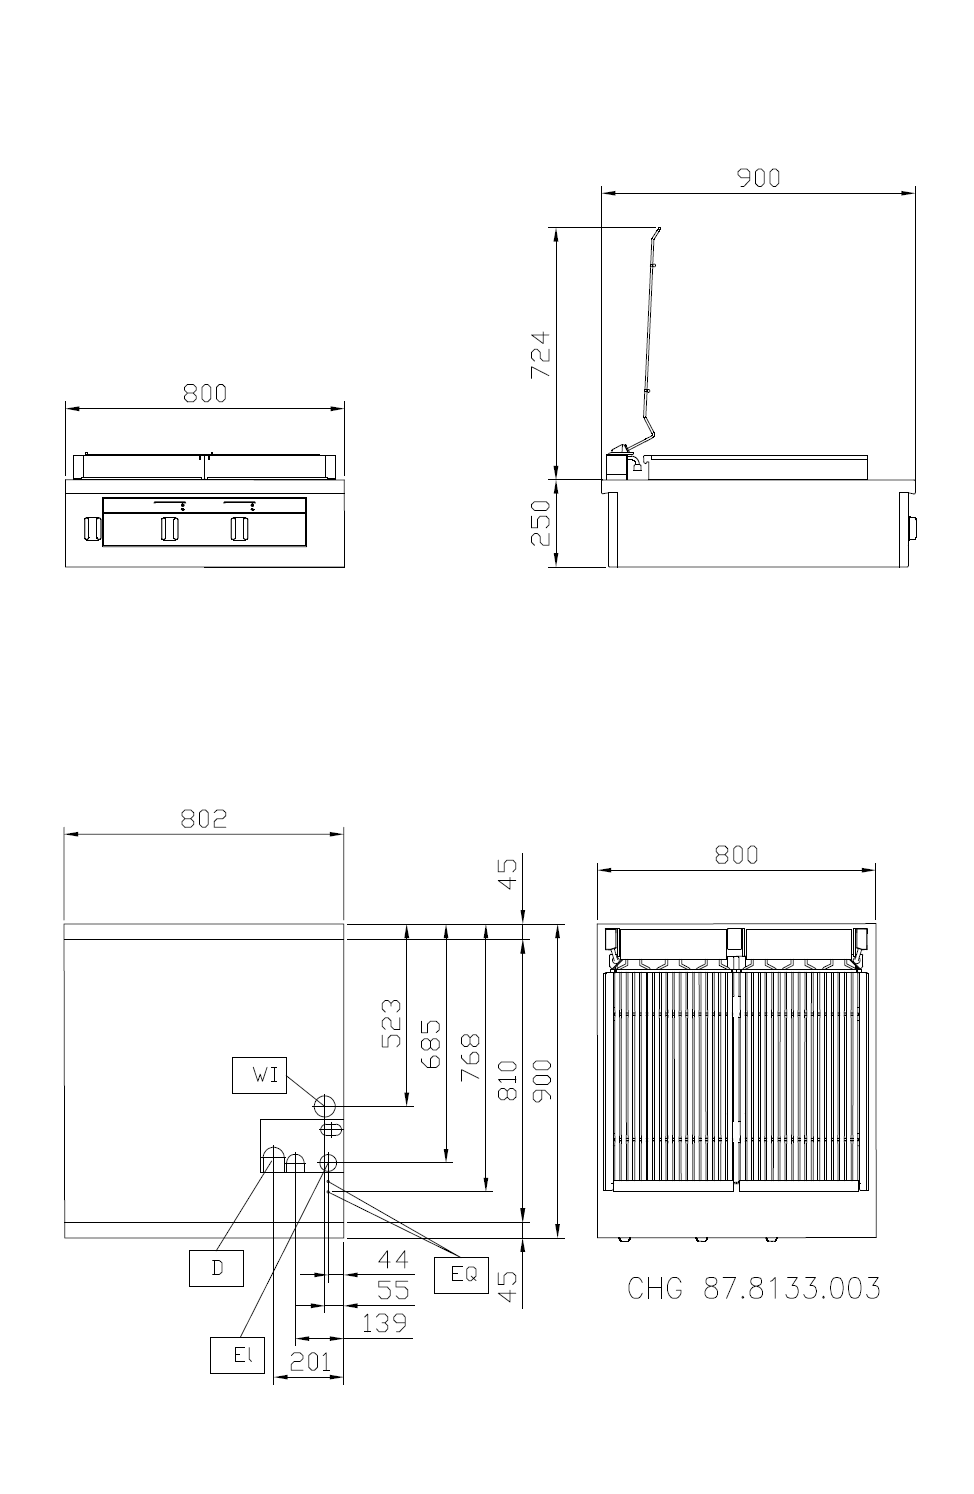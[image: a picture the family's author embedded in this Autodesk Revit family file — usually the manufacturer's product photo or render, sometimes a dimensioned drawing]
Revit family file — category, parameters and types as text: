
# Revit family: QF_ELECTROLUXPROFESSIONAL_589286_MCDEAAHOIO
name_source: partatom
category: Specialty Equipment
revit_build: Autodesk Revit 2018 (Build: 20190510_1515(x64)
units: mm (PartAtom-declared; Revit-internal decimal feet)

## family parameters
Always vertical = Yes
Cut with Voids When Loaded = No
Part Type = Normal
Room Calculation Point = No
Round Connector Dimension = Use Diameter
Shared = No
Work Plane-Based = No

## types (1)
- Standard
    Accessory = Yes
    Cold Water Size = 1"
    Compressed Air Pressure = 0.00 psi
    Compressed Air Size = 0"
    Compressed Air Volume = 0 GPM
    Condensate Return Size = 0"
    Cycle = 60 Hz
    Depth Actual = 900 mm
    Description = ELECTRIC CHARGRILL, 1 SIDE, 800X900X250H
    Direct Waste Size = 1"
    Gas Input Pressure = 0.0
    Gas KW = 0
    Gas Size = 0"
    HP = 14.5 HP
    Height Actual = 250 mm  [stored 0.82021 ft]
    Hot Water Size = 0"
    Item Number = 589286
    Length Actual = 800 mm  [stored 2.62467 ft]
    Manufacturer = Electrolux Professional
    Model = MCDEAAHOIO
    Phase = 3
    Refrigerant Compressor Remote = Yes
    Refrigeration Liquid Line Size = 0"
    Refrigeration Suction Line Size = 0"
    Steam Pounds per Hour = 0
    Steam Supply Maximum Pressure = 0.00 psi
    Steam Supply Minimum Pressure = 0.00 psi
    Steam Supply Size = 0"
    URL = http://professional.electrolux.com
    URL Manufacturer = http://professional.electrolux.com
    Volts = 400 V
    Watts = 0 W
    Weight = 40.82 kg

note: source unit labels omitted for Gas Input Pressure — the stored unit's dimension contradicts the parameter name (converter mislabeling)

note: [stored X ft] marks values corroborated as IEEE doubles in the binary element streams (Revit-internal decimal feet)

## geometry (parser evidence)
native form markers: Sweep x4
no freeform markers — native parametric forms only
